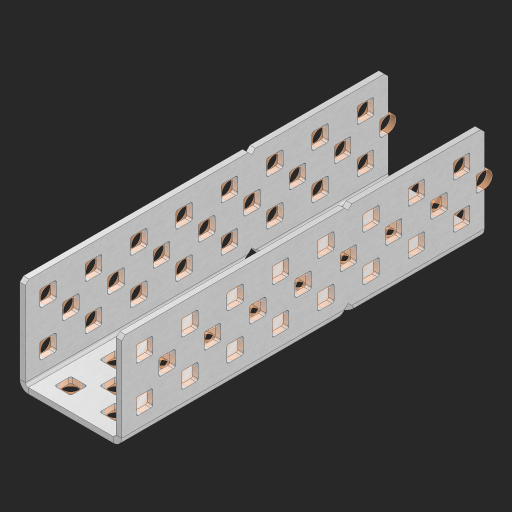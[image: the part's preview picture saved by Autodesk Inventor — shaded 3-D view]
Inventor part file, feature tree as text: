
AUTODESK INVENTOR PART (.ipt)
format: ipt  version: 2023 (Build 270158000, 158)  size: 1,222,144 bytes
history: native  units: in
note: dims shown in document units (in); Inventor stores cm internally (conversion verified against a paired STEP export)
features: other x102, extrude x94, sheet_metal_op x8, sketch x7, mirror x3, pattern_linear x2, chamfer x1
ambient origin geometry x8: Origin, YZ Plane, XZ Plane, XY Plane, X Axis, Y Axis, Z Axis, Center Point
bodies: Solid1 (feature_tree), Body (feature_tree)
feature tree (217):
  sheet_metal_op  "Flanges"
  sheet_metal_op  "Body Pattern"
  pattern_linear  "Center Pattern"  Spacing1=1.0in  [1 undecoded]
  other  "Arc Length"
  mirror  "Notch Mirror"
  pattern_linear  "Notch Pattern"  Spacing1=0.25in  [1 undecoded]
  other  "Diagonal Plane"
  mirror  "Flange 1"
  mirror  "Flange 2"
  chamfer  "End Chamfer"
  sketch  "Sketch1"  dims[d0=1.0in]
  other  "Plate1"
  sketch  "Sketch2"  dims[d1=4.0in]
  other  "Plate2"
  sheet_metal_op  "Bend1"
  sheet_metal_op  "Corner1"
  sketch  "Sketch8"  dims[d2=0.0625in]
  sketch  "Sketch9"  dims[d3=0.0625in]
  other  "Srf91"
  sheet_metal_op  "Body Pattern Sketch"
  other  "Srf92"
  sketch  "Sketch13"  dims[d4=0.0312in]
  sketch  "Sketch15"  dims[d5=0.125in]
  sketch  "Sketch16"  dims[d6=0.0625in d7=1.0in d8=90.0deg d9=0.0312in d10=0.25in d11=0.0625in d12=0.0625in d49=0.182in d50=0.02in d52=0.25in d53=0.0625in d54=0.0in d55=0.172in d56=1.0in d57=0.0in d60=3.1496in d62=0.5in d63=0.7874in d65=0.5in d85=0.1473in d86=0.1782in d88=0.04in d89=0.0625in d90=0.0in d91=0.04in d92=0.0491in d95=2.5in d96=0.04in d97=0.25in d98=45.0deg d99=0.25in d102=2.497in d106=0.182in d107=0.02in d108=0.5in d110=0.0625in d111=0.0in d112=0.172in d113=0.5in d114=0.0in d117=0.5in d118=0.5in d131=0.25in d132=0.25in]
  other  "Srf786"
  other  "Srf889"
  other  "Srf890"
  other  "Srf891"
  other  "Srf892"
  other  "Srf893"
  other  "Srf894"
  other  "Srf895"
  other  "Srf1315"
  other  "Srf1316"
  other  "Srf1317"
  other  "Srf1325"
  other  "Srf1326"
  other  "Srf1327"
  other  "Srf1328"
  other  "Srf1329"
  other  "Srf1330"
  other  "Srf1331"
  other  "Srf1374"
  other  "Srf1375"
  other  "Srf1376"
  other  "Srf1384"
  other  "Srf1385"
  other  "Srf1386"
  other  "Srf1387"
  other  "Srf1388"
  other  "Srf1389"
  other  "Srf1390"
  other  "Srf1433"
  other  "Srf1434"
  other  "Srf1473"
  other  "Srf1474"
  other  "Srf1475"
  other  "Srf1476"
  other  "Srf1477"
  other  "Srf1478"
  other  "Srf1479"
  other  "Srf1480"
  other  "Srf1500"
  other  "Srf1501"
  other  "Srf1502"
  other  "Srf1503"
  other  "Srf1504"
  other  "Srf1505"
  other  "Srf1506"
  other  "Srf1507"
  other  "Srf1508"
  other  "Srf1509"
  other  "Srf1510"
  other  "Srf1511"
  other  "Srf1512"
  other  "Srf1513"
  other  "Srf1538"
  other  "Srf1539"
  other  "Srf1540"
  other  "Srf1541"
  other  "Srf1542"
  other  "Srf1543"
  other  "Srf1544"
  other  "Srf1545"
  other  "Srf1546"
  other  "Srf1547"
  other  "Srf1548"
  other  "Srf1549"
  other  "Srf1550"
  other  "Srf1551"
  other  "Srf1576"
  other  "Srf1577"
  other  "Srf1578"
  other  "Srf1579"
  other  "Srf1580"
  other  "Srf1581"
  other  "Srf1582"
  other  "Srf1583"
  other  "Srf1584"
  other  "Srf1585"
  other  "Srf1586"
  other  "Srf1587"
  other  "Srf1588"
  other  "Srf1589"
  other  "Srf1614"
  other  "Srf1615"
  other  "Srf1616"
  other  "Srf1617"
  other  "Srf1618"
  other  "Srf1619"
  other  "Srf1620"
  other  "Srf1621"
  other  "Srf1622"
  other  "Srf1623"
  other  "Srf1624"
  other  "Srf1625"
  other  "Srf1626"
  other  "Srf1627"
  sheet_metal_op  "Body Stamp"
  sheet_metal_op  "Body Circle"
  other  "Center Stamp"
  other  "Center Circle"
  sheet_metal_op  "Notch"
  extrude  "ExtrusionSrf92"  Depth=0.0625in
  extrude  "ExtrusionSrf889"  Depth=0.0625in
  extrude  "ExtrusionSrf890"  Depth=0.182in
  extrude  "ExtrusionSrf891"  Depth=0.02in
  extrude  "ExtrusionSrf892"  Depth=0.25in
  extrude  "ExtrusionSrf893"  Depth=0.0625in
  extrude  "ExtrusionSrf894"  TaperAngle=0.0deg  [1 undecoded]
  extrude  "ExtrusionSrf895"  Depth=0.25in
  extrude  "ExtrusionSrf1315"  Depth=1.0in TaperAngle=0.0deg
  extrude  "ExtrusionSrf1316"  Depth=0.25in
  extrude  "ExtrusionSrf1355"  Depth=0.5in
  extrude  "ExtrusionSrf1356"  Depth=0.25in
  extrude  "ExtrusionSrf1357"  Depth=0.25in
  extrude  "ExtrusionSrf1358"  Depth=0.25in
  extrude  "ExtrusionSrf1359"  Depth=0.0625in
  extrude  "ExtrusionSrf1360"  TaperAngle=0.0deg  [1 undecoded]
  extrude  "ExtrusionSrf1361"  Depth=0.25in
  extrude  "ExtrusionSrf1362"  Depth=0.25in
  extrude  "ExtrusionSrf1374"  Depth=2.5in
  extrude  "ExtrusionSrf1375"  Depth=0.25in TaperAngle=45.0deg
  extrude  "ExtrusionSrf1414"  Depth=0.25in
  extrude  "ExtrusionSrf1415"  Depth=0.25in
  extrude  "ExtrusionSrf1416"  Depth=0.182in
  extrude  "ExtrusionSrf1417"  Depth=0.02in
  extrude  "ExtrusionSrf1418"  Depth=0.5in
  extrude  "ExtrusionSrf1419"  Depth=0.0625in
  extrude  "ExtrusionSrf1420"  TaperAngle=0.0deg  [1 undecoded]
  extrude  "ExtrusionSrf1421"  Depth=0.25in
  extrude  "ExtrusionSrf1433"  Depth=0.5in TaperAngle=0.0deg
  extrude  "ExtrusionSrf1434"  Depth=0.5in
  extrude  "ExtrusionSrf1473"  Depth=0.5in
  extrude  "ExtrusionSrf1474"  Depth=0.25in
  extrude  "ExtrusionSrf1475"  Depth=0.25in
  extrude  "ExtrusionSrf1476"  [1 undecoded]
  extrude  "ExtrusionSrf1477"  [1 undecoded]
  extrude  "ExtrusionSrf1478"  [1 undecoded]
  extrude  "ExtrusionSrf1479"  [1 undecoded]
  extrude  "ExtrusionSrf1480"  [1 undecoded]
  extrude  "ExtrusionSrf1500"  [1 undecoded]
  extrude  "ExtrusionSrf1501"  [1 undecoded]
  extrude  "ExtrusionSrf1502"  [1 undecoded]
  extrude  "ExtrusionSrf1503"  [1 undecoded]
  extrude  "ExtrusionSrf1504"  [1 undecoded]
  extrude  "ExtrusionSrf1505"  [1 undecoded]
  extrude  "ExtrusionSrf1506"  [1 undecoded]
  extrude  "ExtrusionSrf1507"  [1 undecoded]
  extrude  "ExtrusionSrf1508"  [1 undecoded]
  extrude  "ExtrusionSrf1509"  [1 undecoded]
  extrude  "ExtrusionSrf1510"  [1 undecoded]
  extrude  "ExtrusionSrf1511"  [1 undecoded]
  extrude  "ExtrusionSrf1512"  [1 undecoded]
  extrude  "ExtrusionSrf1513"  [1 undecoded]
  extrude  "ExtrusionSrf1538"  [1 undecoded]
  extrude  "ExtrusionSrf1539"  [1 undecoded]
  extrude  "ExtrusionSrf1540"  [1 undecoded]
  extrude  "ExtrusionSrf1541"  [1 undecoded]
  extrude  "ExtrusionSrf1542"  [1 undecoded]
  extrude  "ExtrusionSrf1543"  [1 undecoded]
  extrude  "ExtrusionSrf1544"  [1 undecoded]
  extrude  "ExtrusionSrf1545"  [1 undecoded]
  extrude  "ExtrusionSrf1546"  [1 undecoded]
  extrude  "ExtrusionSrf1547"  [1 undecoded]
  extrude  "ExtrusionSrf1548"  [1 undecoded]
  extrude  "ExtrusionSrf1549"  [1 undecoded]
  extrude  "ExtrusionSrf1550"  [1 undecoded]
  extrude  "ExtrusionSrf1551"  [1 undecoded]
  extrude  "ExtrusionSrf1576"  [1 undecoded]
  extrude  "ExtrusionSrf1577"  [1 undecoded]
  extrude  "ExtrusionSrf1578"  [1 undecoded]
  extrude  "ExtrusionSrf1579"  [1 undecoded]
  extrude  "ExtrusionSrf1580"  [1 undecoded]
  extrude  "ExtrusionSrf1581"  [1 undecoded]
  extrude  "ExtrusionSrf1582"  [1 undecoded]
  extrude  "ExtrusionSrf1583"  [1 undecoded]
  extrude  "ExtrusionSrf1584"  [1 undecoded]
  extrude  "ExtrusionSrf1585"  [1 undecoded]
  extrude  "ExtrusionSrf1586"  [1 undecoded]
  extrude  "ExtrusionSrf1587"  [1 undecoded]
  extrude  "ExtrusionSrf1588"  [1 undecoded]
  extrude  "ExtrusionSrf1589"  [1 undecoded]
  extrude  "ExtrusionSrf1614"  [1 undecoded]
  extrude  "ExtrusionSrf1615"  [1 undecoded]
  extrude  "ExtrusionSrf1616"  [1 undecoded]
  extrude  "ExtrusionSrf1617"  [1 undecoded]
  extrude  "ExtrusionSrf1618"  [1 undecoded]
  extrude  "ExtrusionSrf1619"  [1 undecoded]
  extrude  "ExtrusionSrf1620"  [1 undecoded]
  extrude  "ExtrusionSrf1621"  [1 undecoded]
  extrude  "ExtrusionSrf1622"  [1 undecoded]
  extrude  "ExtrusionSrf1623"  [1 undecoded]
  extrude  "ExtrusionSrf1624"  [1 undecoded]
  extrude  "ExtrusionSrf1625"  [1 undecoded]
  extrude  "ExtrusionSrf1626"  [1 undecoded]
  extrude  "ExtrusionSrf1627"  [1 undecoded]
note: 66 required parameter values undecoded (feature->parameter linkage not recoverable at this tier; creation-order binding heuristic only, values carry confidence <= 0.55)
